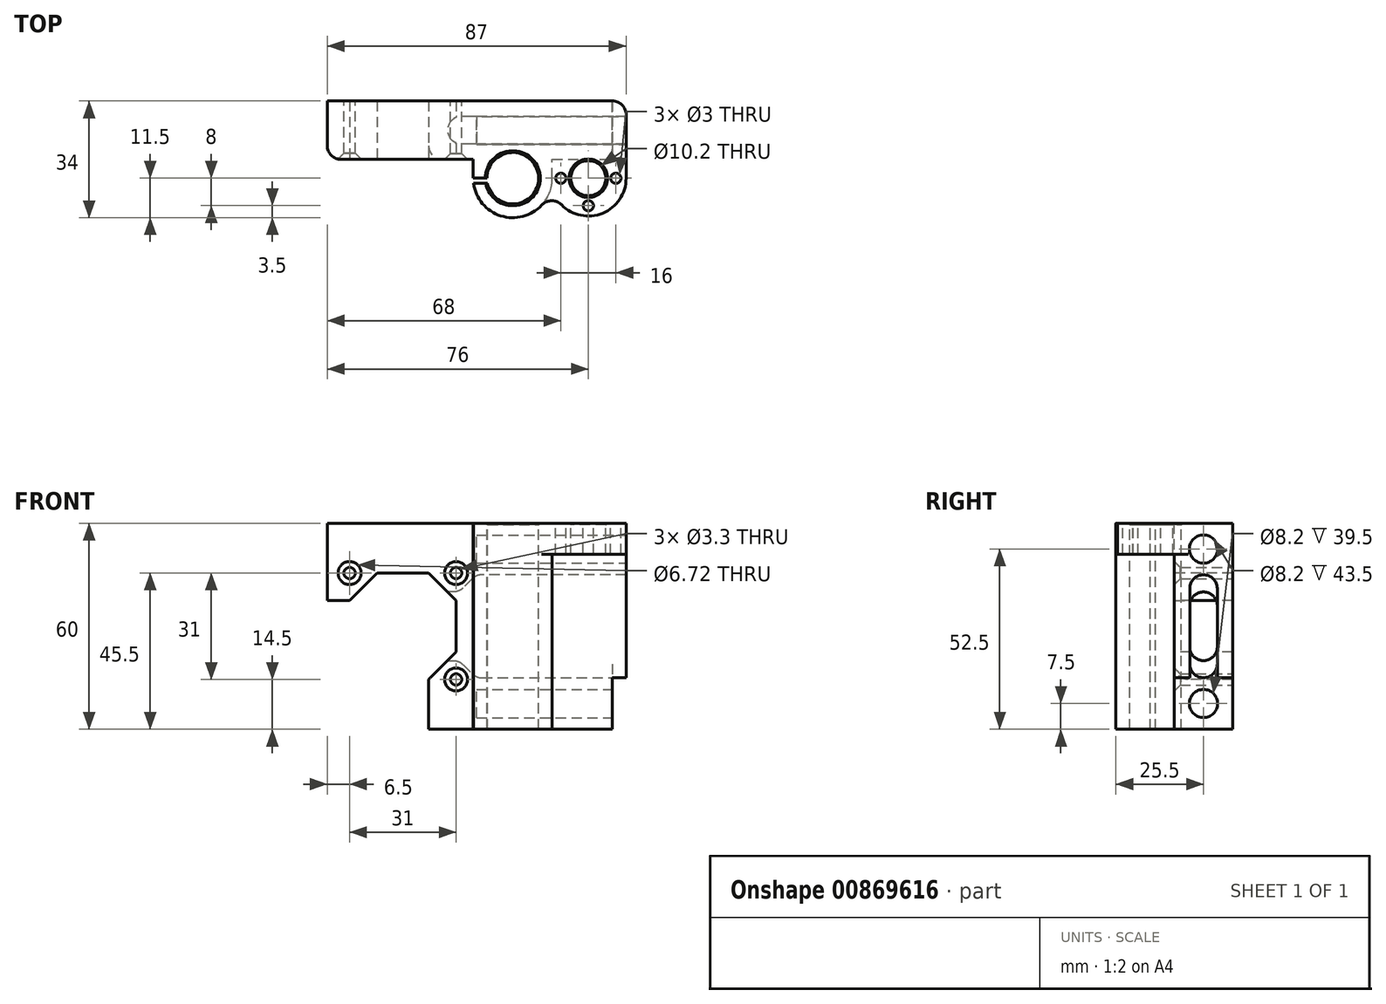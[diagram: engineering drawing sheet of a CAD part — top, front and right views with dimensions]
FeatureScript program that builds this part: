
annotation { "Feature Type Name" : "Feature", "Feature Type Description" : "" }
export const myFeature = defineFeature(function(context is Context, id is Id, definition is map)
    precondition{}
    {
        {
            var Q0;
            Q0=qCreatedBy(makeId("Top.planeOp"),FACE);
            var sketch = newSketch(context, id + "F0", { "sketchPlane" : qUnion([Q0])});
            skArc(sketch, "E0", {"start": v(-7.35, -1.5) * mm, "mid": v(7.46, 0.75) * mm, "end": v(-7.5, 0) * mm});
            skArc(sketch, "E1.0", {"start": v(-11.4, -1.5) * mm, "mid": v(0.75, -11.48) * mm, "end": v(11.5, 0) * mm});
            skCircle(sketch, "E2", {"center": v(22, 0) * mm, "radius": 5.1 * mm});
            skArc(sketch, "E3", {"start": v(14.19, -7.74) * mm, "mid": v(26.19, -10.17) * mm, "end": v(33, 0) * mm});
            skLineSegment(sketch, "E4", {"start": v(-61.05, 14) * mm, "end": v(37.89, 14) * mm, "construction": true});
            skCircle(sketch, "E5", {"center": v(22, 0) * mm, "radius": 8 * mm, "construction": true});
            skLineSegment(sketch, "E6", {"start": v(33, 0) * mm, "end": v(33, 22.5) * mm});
            skLineSegment(sketch, "E7", {"start": v(33, 22.5) * mm, "end": v(-54, 22.5) * mm});
            skLineSegment(sketch, "E8", {"start": v(-54, 22.5) * mm, "end": v(-54, 5.5) * mm});
            skLineSegment(sketch, "E9", {"start": v(-54, 5.5) * mm, "end": v(-11.5, 5.5) * mm});
            skLineSegment(sketch, "E10", {"start": v(-11.5, 5.5) * mm, "end": v(-11.5, 0) * mm});
            skArc(sketch, "E11", {"start": v(14.19, -7.74) * mm, "mid": v(11.28, -6.56) * mm, "end": v(8.42, -7.83) * mm});
            skLineSegment(sketch, "E12", {"start": v(11.5, 0) * mm, "end": v(11.5, 5.5) * mm});
            skLineSegment(sketch, "E13", {"start": v(11.5, 5.5) * mm, "end": v(33, 5.5) * mm});
            skCircle(sketch, "E14", {"center": v(14, 0) * mm, "radius": 1.5 * mm});
            skCircle(sketch, "E15.1.0", {"center": v(22, -8) * mm, "radius": 1.5 * mm});
            skCircle(sketch, "E15.2.0", {"center": v(30, 0) * mm, "radius": 1.5 * mm});
            skLineSegment(sketch, "E15.anchor1", {"start": v(22, 0) * mm, "end": v(14, 0) * mm, "construction": true});
            skLineSegment(sketch, "E15.anchor2", {"start": v(22, 0) * mm, "end": v(30, 0) * mm, "construction": true});
            skLineSegment(sketch, "E16", {"start": v(-7.5, 0) * mm, "end": v(-11.5, 0) * mm});
            skLineSegment(sketch, "E17", {"start": v(-7.35, -1.5) * mm, "end": v(-11.5, -1.5) * mm});
            skSolve(sketch);
        }
        {
            var Q0;
            Q0=makeQuery(id+"F0.imprint","IMPRINT",FACE,{"disambiguationData":[TD([[makeQuery(id+"F0.imprint","IMPRINT",EDGE,{"derivedFrom":sQuery(id+"F0.wireOp",EDGE,"E0")}),-1.0]])]});
            extrude(context, id + "F1", {"entities" : qUnion([Q0]), "oppositeDirection" : true, "depth" : 60 * mm, "offsetDistance" : 25 * mm});
        }
        {
            var Q0;
            Q0 = qSketchRegion(id + "F0", true);
            extrude(context, id + "F2", {"entities" : qUnion([Q0]), "operationType" : NewBodyOperationType.ADD, "oppositeDirection" : true, "depth" : 9 * mm, "offsetDistance" : 25 * mm});
        }
        {
            var Q0;
            Q0=makeQuery(id+"F1.opExtrude","SWEPT_EDGE",EDGE,{"disambiguationData":[OSD([sQuery(id+"F0.wireOp",EDGE,"E8"),sQuery(id+"F0.wireOp",EDGE,"E9")])]});
            var Q1;
            Q1=makeQuery(id+"F1.opExtrude","SWEPT_EDGE",EDGE,{"disambiguationData":[OSD([sQuery(id+"F0.wireOp",EDGE,"E6"),sQuery(id+"F0.wireOp",EDGE,"E13")])]});
            var Q2;
            Q2=makeQuery(id+"F1.opExtrude","SWEPT_EDGE",EDGE,{"disambiguationData":[OSD([sQuery(id+"F0.wireOp",EDGE,"E6"),sQuery(id+"F0.wireOp",EDGE,"E7")])]});
            fillet(context, id + "F3", {"entities" : qUnion([Q0, Q1, Q2]), "radius" : 4 * mm, "tangentPropagation" : true, "allowEdgeOverflow" : false});
        }
        {
            var Q0;
            Q0=qCreatedBy(makeId("Front.planeOp"),FACE);
            var sketch = newSketch(context, id + "F4", { "sketchPlane" : qUnion([Q0])});
            skCircle(sketch, "E18", {"center": v(-32, -30) * mm, "radius": 15.5 * mm, "construction": true});
            skLineSegment(sketch, "E19", {"start": v(-57.77, -22.5) * mm, "end": v(-47.5, -22.5) * mm});
            skLineSegment(sketch, "E20", {"start": v(-47.5, -22.5) * mm, "end": v(-39.5, -14.5) * mm});
            skLineSegment(sketch, "E21", {"start": v(-39.5, -14.5) * mm, "end": v(-24.5, -14.5) * mm});
            skLineSegment(sketch, "E22", {"start": v(-24.5, -14.5) * mm, "end": v(-16.5, -22.5) * mm});
            skLineSegment(sketch, "E23", {"start": v(-16.5, -22.5) * mm, "end": v(-16.5, -37.5) * mm});
            skLineSegment(sketch, "E24", {"start": v(-16.5, -37.5) * mm, "end": v(-24.5, -45.5) * mm});
            skLineSegment(sketch, "E25", {"start": v(-24.5, -45.5) * mm, "end": v(-24.5, -64.37) * mm});
            skLineSegment(sketch, "E26", {"start": v(-24.5, -64.37) * mm, "end": v(-57.77, -64.37) * mm});
            skLineSegment(sketch, "E27", {"start": v(-57.77, -64.37) * mm, "end": v(-57.77, -22.5) * mm});
            skLineSegment(sketch, "E28.bottom", {"start": v(36.46, -61.87) * mm, "end": v(29, -61.87) * mm});
            skLineSegment(sketch, "E28.top", {"start": v(36.46, -45) * mm, "end": v(29, -45) * mm});
            skLineSegment(sketch, "E28.left", {"start": v(36.46, -61.87) * mm, "end": v(36.46, -45) * mm});
            skLineSegment(sketch, "E28.right", {"start": v(29, -61.87) * mm, "end": v(29, -45) * mm});
            skSolve(sketch);
        }
        {
            var Q0;
            Q0 = qSketchRegion(id + "F4", true);
            extrude(context, id + "F5", {"entities" : qUnion([Q0]), "operationType" : NewBodyOperationType.REMOVE, "endBound" : BoundingType.THROUGH_ALL, "oppositeDirection" : true, "depth" : 25 * mm, "offsetDistance" : 25 * mm});
        }
        {
            var Q0;
            {var subQ0=sQuery(id+"F0.wireOp",EDGE,"E6");Q0=makeQuery(id+"F2.boolean.opBoolean","MERGE",FACE,{"derivedFrom":[makeQuery(id+"F1.opExtrude","SWEPT_FACE",FACE,{"disambiguationData":[OSD([subQ0])]}),makeQuery(id+"F2.opExtrude","SWEPT_FACE",FACE,{"disambiguationData":[OSD([subQ0])]})]});}
            var sketch = newSketch(context, id + "F6", { "sketchPlane" : qUnion([Q0])});
            skCircle(sketch, "E29", {"center": v(14, -7.5) * mm, "radius": 4.1 * mm});
            skCircle(sketch, "E30", {"center": v(14, -52.5) * mm, "radius": 4.1 * mm});
            skSolve(sketch);
        }
        {
            var Q0;
            Q0 = qSketchRegion(id + "F6", true);
            extrude(context, id + "F7", {"entities" : qUnion([Q0]), "operationType" : NewBodyOperationType.REMOVE, "oppositeDirection" : true, "depth" : 43.5 * mm, "offsetDistance" : 25 * mm});
        }
        {
            var Q0;
            Q0=qCreatedBy(makeId("Front.planeOp"),FACE);
            cPlane(context, id + "F8", {"entities" : qUnion([Q0]), "cplaneType" : CPlaneType.OFFSET, "offset" : 14 * mm, "oppositeDirection" : true, "width" : 150 * mm, "height" : 150 * mm});
        }
        {
            var Q0;
            Q0=qCreatedBy(id+"F8.planeOp",FACE);
            var sketch = newSketch(context, id + "F9", { "sketchPlane" : qUnion([Q0])});
            skLineSegment(sketch, "E31", {"start": v(-21.87, -20) * mm, "end": v(-17.31, -20) * mm});
            skLineSegment(sketch, "E32", {"start": v(-14.49, -18.83) * mm, "end": v(-11.83, -16.17) * mm});
            skLineSegment(sketch, "E33", {"start": v(-9, -15) * mm, "end": v(34.4, -15) * mm});
            skLineSegment(sketch, "E34", {"start": v(34.4, -15) * mm, "end": v(34.4, -45) * mm});
            skLineSegment(sketch, "E35", {"start": v(34.4, -45) * mm, "end": v(-9, -45) * mm});
            skLineSegment(sketch, "E36", {"start": v(-11.83, -43.83) * mm, "end": v(-14.49, -41.17) * mm});
            skLineSegment(sketch, "E37", {"start": v(-17.31, -40) * mm, "end": v(-21.87, -40) * mm});
            skLineSegment(sketch, "E38", {"start": v(-21.87, -40) * mm, "end": v(-21.87, -20) * mm});
            skPoint(sketch, "E39.visualSharp", {"position": v(-10.66, -45) * mm});
            skArc(sketch, "E39.filletArc", {"start": v(-11.83, -43.83) * mm, "mid": v(-10.53, -44.7) * mm, "end": v(-9, -45) * mm});
            skPoint(sketch, "E40.visualSharp", {"position": v(-15.66, -40) * mm});
            skArc(sketch, "E40.filletArc", {"start": v(-14.49, -41.17) * mm, "mid": v(-15.78, -40.3) * mm, "end": v(-17.31, -40) * mm});
            skPoint(sketch, "E41.visualSharp", {"position": v(-10.66, -15) * mm});
            skArc(sketch, "E41.filletArc", {"start": v(-9, -15) * mm, "mid": v(-10.53, -15.3) * mm, "end": v(-11.83, -16.17) * mm});
            skPoint(sketch, "E42.visualSharp", {"position": v(-15.66, -20) * mm});
            skArc(sketch, "E42.filletArc", {"start": v(-17.31, -20) * mm, "mid": v(-15.78, -19.7) * mm, "end": v(-14.49, -18.83) * mm});
            skSolve(sketch);
        }
        {
            var Q0;
            Q0=makeQuery(id+"F1.opExtrude","SWEPT_FACE",FACE,{"disambiguationData":[OSD([sQuery(id+"F0.wireOp",EDGE,"E9")])]});
            var sketch = newSketch(context, id + "F10", { "sketchPlane" : qUnion([Q0])});
            skPoint(sketch, "E43", {"position": v(-47.5, -14.5) * mm});
            skPoint(sketch, "E44", {"position": v(-16.5, -14.5) * mm});
            skPoint(sketch, "E45", {"position": v(-16.5, -45.5) * mm});
            skSolve(sketch);
        }
        {
            var Q0;
            Q0=sQuery(id+"F10.wireOp",VERTEX,"E43");
            var Q1;
            Q1=sQuery(id+"F10.wireOp",VERTEX,"E45");
            var Q2;
            Q2=sQuery(id+"F10.wireOp",VERTEX,"E44");
            var Q3;
            Q3=makeQuery(id+"F1.opExtrude","SWEPT_BODY",BODY,{"disambiguationData":[OSD([sQuery(id+"F0.wireOp",EDGE,"E0"),sQuery(id+"F0.wireOp",EDGE,"E1.0"),sQuery(id+"F0.wireOp",EDGE,"E6"),sQuery(id+"F0.wireOp",EDGE,"E7"),sQuery(id+"F0.wireOp",EDGE,"E8"),sQuery(id+"F0.wireOp",EDGE,"E9"),sQuery(id+"F0.wireOp",EDGE,"E10"),sQuery(id+"F0.wireOp",EDGE,"E12"),sQuery(id+"F0.wireOp",EDGE,"E13")])]});
            hole(context, id + "F11", {"style" : HoleStyle.C_SINK, "endStyle" : HoleEndStyle.BLIND, "standardTappedOrClearance" : lookupTablePath({ "fit" : "Normal", "standard" : "ISO", "size" : "M3", "type" : "Clearance" }), "standardBlindInLast" : lookupTablePath({ "fit" : "Standard", "standard" : "ISO", "size" : "M3", "type" : "Clearance" }), "holeDiameter" : 3.3 * mm, "cSinkDiameter" : 6.72 * mm, "cSinkAngle" : 90 * degree, "majorDiameter" : 5 * mm, "holeDepth" : 20 * mm, "isTappedThrough" : true, "tappedDepth" : 12 * mm, "tapClearance" : 3, "locations" : qUnion([Q0, Q1, Q2]), "scope" : qUnion([Q3])});
        }
        {
            var Q0;
            Q0 = qSketchRegion(id + "F9", true);
            extrude(context, id + "F12", {"entities" : qUnion([Q0]), "operationType" : NewBodyOperationType.REMOVE, "depth" : 8 * mm, "offsetDistance" : 25 * mm, "symmetric" : true});
        }
        {
            var Q0;
            Q0=makeQuery(id+"F5.boolean.opBoolean","INTERSECT",EDGE,{"derivedFrom":[makeQuery(id+"F1.opExtrude","SWEPT_FACE",FACE,{"disambiguationData":[OSD([sQuery(id+"F0.wireOp",EDGE,"E9")])]}),makeQuery(id+"F5.opExtrude","SWEPT_FACE",FACE,{"disambiguationData":[OSD([sQuery(id+"F4.wireOp",EDGE,"E25")])]})]});
            fillet(context, id + "F13", {"entities" : qUnion([Q0]), "radius" : 4 * mm, "tangentPropagation" : true, "allowEdgeOverflow" : false});
        }
        {
            var Q0;
            Q0=makeQuery(id+"F1.opExtrude","CAP_EDGE",EDGE,{"disambiguationData":[OSD([sQuery(id+"F0.wireOp",EDGE,"E0")])],"isStart":true});
            var Q1;
            Q1=makeQuery(id+"F2.opExtrude","CAP_EDGE",EDGE,{"disambiguationData":[OSD([sQuery(id+"F0.wireOp",EDGE,"E2")])],"isStart":true});
            chamfer(context, id + "F14", {"entities" : qUnion([Q0, Q1]), "chamferType" : ChamferType.TWO_OFFSETS, "width1" : 0.4 * mm, "oppositeDirection" : false, "width2" : 0.5 * mm, "tangentPropagation" : true});
        }
        {
            var Q0;
            Q0=makeQuery(id+"F12.boolean.opBoolean","COPY",EDGE,{"derivedFrom":makeQuery(id+"F12.opExtrude","CAP_EDGE",EDGE,{"disambiguationData":[OSD([sQuery(id+"F9.wireOp",EDGE,"E33")])],"isStart":false})});
            var Q1;
            Q1=makeQuery(id+"F12.boolean.opBoolean","COPY",EDGE,{"derivedFrom":makeQuery(id+"F12.opExtrude","CAP_EDGE",EDGE,{"disambiguationData":[OSD([sQuery(id+"F9.wireOp",EDGE,"E33")])],"isStart":true})});
            var Q2;
            {var subQ0=sQuery(id+"F9.wireOp",EDGE,"E35");Q2=makeQuery(id+"F12.boolean.opBoolean","COPY",EDGE,{"disambiguationData":[topologyDisambiguationEdgeConnected([makeQuery(id+"F12.opExtrude","SWEPT_FACE",FACE,{"disambiguationData":[OSD([subQ0])]})])],"derivedFrom":makeQuery(id+"F12.opExtrude","CAP_EDGE",EDGE,{"disambiguationData":[OSD([subQ0])],"isStart":false})});}
            var Q3;
            {var subQ0=sQuery(id+"F9.wireOp",EDGE,"E35");Q3=makeQuery(id+"F12.boolean.opBoolean","COPY",EDGE,{"disambiguationData":[topologyDisambiguationEdgeConnected([makeQuery(id+"F12.opExtrude","SWEPT_FACE",FACE,{"disambiguationData":[OSD([subQ0])]})])],"derivedFrom":makeQuery(id+"F12.opExtrude","CAP_EDGE",EDGE,{"disambiguationData":[OSD([subQ0])],"isStart":true})});}
            fillet(context, id + "F15", {"entities" : qUnion([Q0, Q1, Q2, Q3]), "radius" : 4 * mm, "tangentPropagation" : true, "allowEdgeOverflow" : false});
        }
    });
